# Revit family: WENGER 7-SHELF MUSIC LIBRARY SYSTEM - OVERSIZED
name_source: partatom
category: Generic Models
revit_build: Autodesk Revit Architecture 2014 (Build: 20130308_1515(x64)
units: mm (PartAtom-declared; Revit-internal decimal feet)

## types (24) — shared parameters
ECP WIDTH = 0' - 1 1/2"
HEIGHT = 7' - 8"
UNIT SPACING = 1' - 7"

## per-type parameters (varying)
| type | # OF UNITS | Description | ECP SPACING | Keynote | Manufacturer | Model | URL |
| 2-UNIT | 2 | MUSIC LIBRARY SYSTEM | 3' - 2" | WENGER MUSIC LIBRARY SYSTEM | WENGER CORPORATION | 7-SHELF | http://www.wengercorp.com |
| 3-UNIT | 3 |  | 4' - 9" |  |  |  |  |
| 4-UNIT | 4 |  | 6' - 4" |  |  |  |  |
| 5-UNIT | 5 |  | 7' - 11" |  |  |  |  |
| 6-UNIT | 6 |  | 9' - 6" |  |  |  |  |
| 7-UNIT | 7 |  | 11' - 1" |  |  |  |  |
| 8-UNIT | 8 |  | 12' - 8" |  |  |  |  |
| 9-UNIT | 9 |  | 14' - 3" |  |  |  |  |
| 10-UNIT | 10 |  | 15' - 10" |  |  |  |  |
| 11-UNIT | 11 |  | 17' - 5" |  |  |  |  |
| 12-UNIT | 12 |  | 19' - 0" |  |  |  |  |
| 13-UNIT | 13 |  | 20' - 7" |  |  |  |  |
| 14-UNIT | 14 |  | 22' - 2" |  |  |  |  |
| 15-UNIT | 15 |  | 23' - 9" |  |  |  |  |
| 16-UNIT | 16 |  | 25' - 4" |  |  |  |  |
| 17-UNIT | 17 |  | 26' - 11" |  |  |  |  |
| 18-UNIT | 18 |  | 28' - 6" |  |  |  |  |
| 19-UNIT | 19 |  | 30' - 1" |  |  |  |  |
| 20-UNIT | 20 |  | 31' - 8" |  |  |  |  |
| 21-UNIT | 21 |  | 33' - 3" |  |  |  |  |
| 22-UNIT | 22 |  | 34' - 10" |  |  |  |  |
| 23-UNIT | 23 |  | 36' - 5" |  |  |  |  |
| 24-UNIT | 24 |  | 38' - 0" |  |  |  |  |
| 25-UNIT | 25 |  | 39' - 7" |  |  |  |  |

## geometry (parser evidence)
native form markers: Sweep x4
no freeform markers — native parametric forms only
